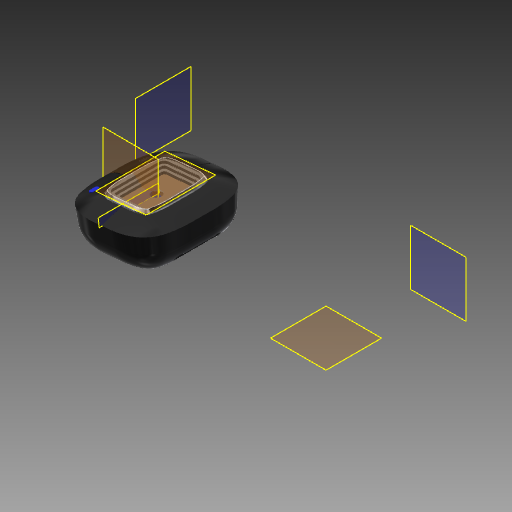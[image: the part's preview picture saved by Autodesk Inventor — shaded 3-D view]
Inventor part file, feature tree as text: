
AUTODESK INVENTOR PART (.ipt)
format: ipt  version: 2017.1 (Build 211199000, 199)  size: 1,797,120 bytes
history: native  units: mm
features: sketch x18, extrude x13, plane x12, fillet x6, sweep x5, other x5, thicken_offset x4, mirror x3, projected_geometry x3
ambient origin geometry x8: Origin, YZ Plane, XZ Plane, XY Plane, X Axis, Y Axis, Z Axis, Center Point
bodies: Body1 (feature_tree), Body2 (feature_tree), Body3 (feature_tree), Body4 (feature_tree), Body5 (feature_tree)
feature tree (69):
  sketch  "Sketch1"  dims[d0=109.0mm d1=44.5mm d189=90.0deg]
  plane  "Work Plane8"
  plane  "Work Plane7"
  sketch  "Sketch3"  dims[d190=3.0mm d193=0.0mm d194=0.0mm]
  plane  "Work Plane6"
  plane  "Work Plane1"
  sketch  "Sketch5"  dims[d201=0.5mm d202=0.5mm]
  plane  "Work Plane2"
  sketch  "Sketch6"  dims[d204=0.5mm d205=0.2mm]
  plane  "Work Plane5"
  sketch  "Sketch8"  dims[d210=15.0mm d211=-0.872665mm d212=10.0mm]
  mirror  "Mirror1"
  thicken_offset  "Thicken1"
  thicken_offset  "Thicken2"
  mirror  "Mirror3"
  thicken_offset  "Thicken4"
  thicken_offset  "Thicken5"
  extrude  "Extrusion6"  Depth=44.5mm
  fillet  "Fillet1"  [1 undecoded]
  sketch  "Sketch12"  dims[d220=5.0mm d221=0.0mm d224=-1.0mm]
  plane  "Work Plane9"
  sweep  "Sweep1"
  mirror  "Mirror4"
  plane  "Work Plane11"
  extrude  "Extrusion9"  Depth=0.5mm
  plane  "Work Plane13"
  extrude  "Extrusion10"  Depth=0.2mm
  plane  "Work Plane14"
  extrude  "Extrusion11"  Depth=10.0mm
  plane  "Work Plane15"
  extrude  "Extrusion12"  [1 undecoded]
  plane  "Work Plane16"
  sketch  "Sketch20"  dims[d242=1.0mm d243=1.0mm]
  extrude  "Extrusion13"  [1 undecoded]
  extrude  "Extrusion15"  Depth=11.0mm
  sketch  "Sketch21"  dims[d245=1.0mm d246=1.0mm d247=1.0mm d248=0.0mm d249=0.0mm]
  extrude  "Extrusion16"  Depth=8.0mm
  fillet  "Fillet2"  Radius=2.0mm
  sketch  "Sketch22"  dims[d250=3.0mm d251=0.0mm d255=2.75mm d256=0.0mm]
  extrude  "Extrusion17"  [1 undecoded]
  extrude  "Extrusion18"  Depth=6.0mm TaperAngle=0.0deg
  fillet  "Fillet3"  [1 undecoded]
  extrude  "Extrusion19"  Depth=1.0mm
  fillet  "Fillet4"  Radius=1.0mm
  extrude  "Extrusion20"  Depth=1.0mm
  extrude  "Extrusion21"  Depth=1.0mm
  fillet  "Fillet5"  Radius=1.0mm
  fillet  "Fillet6"  [1 undecoded]
  other  "Image4"
  other  "Srf3"
  other  "Srf4"
  other  "Srf7"
  other  "Srf8"
  sketch  "Sketch11"  dims[d213=0.0mm d214=0.0mm d219=-0.5mm]
  sketch  "Sketch13"  dims[d225=22.0mm d226=11.0mm]
  sketch  "Sketch15"  dims[d227=16.0mm d228=8.0mm d229=2.0mm]
  projected_geometry  "Projected Loop7"
  sketch  "Sketch17"  dims[d230=1.0mm d231=0.0mm d232=-1.0mm]
  sketch  "Sketch18"  dims[d233=1.0mm d234=6.0mm d235=0.0mm d236=-1.0mm]
  sketch  "Sketch19"  dims[d237=1.0mm d240=1.0mm d241=1.0mm]
  sketch  "Sketch23"  dims[d257=2.0mm d258=0.0mm d259=0.1mm]
  sketch  "Sketch24"  dims[d260=2.1mm d261=0.0mm d262=2.75mm d263=0.0mm]
  sketch  "Sketch25"  dims[d264=0.1mm d265=1.5mm d266=0.0mm d267=0.5mm d268=10.0mm d269=0.0mm d270=5.0mm d271=5.0mm d272=0.0mm d273=3.0mm d274=0.5mm d275=15.0mm d276=14.0mm]
  projected_geometry  "Projected Loop10"
  sweep  "SweepSrf1"
  sweep  "SweepSrf2"
  sweep  "SweepSrf5"
  sweep  "SweepSrf6"
  projected_geometry  "Project Cut Edges1"
note: 6 required parameter values undecoded (feature->parameter linkage not recoverable at this tier; creation-order binding heuristic only, values carry confidence <= 0.55)
